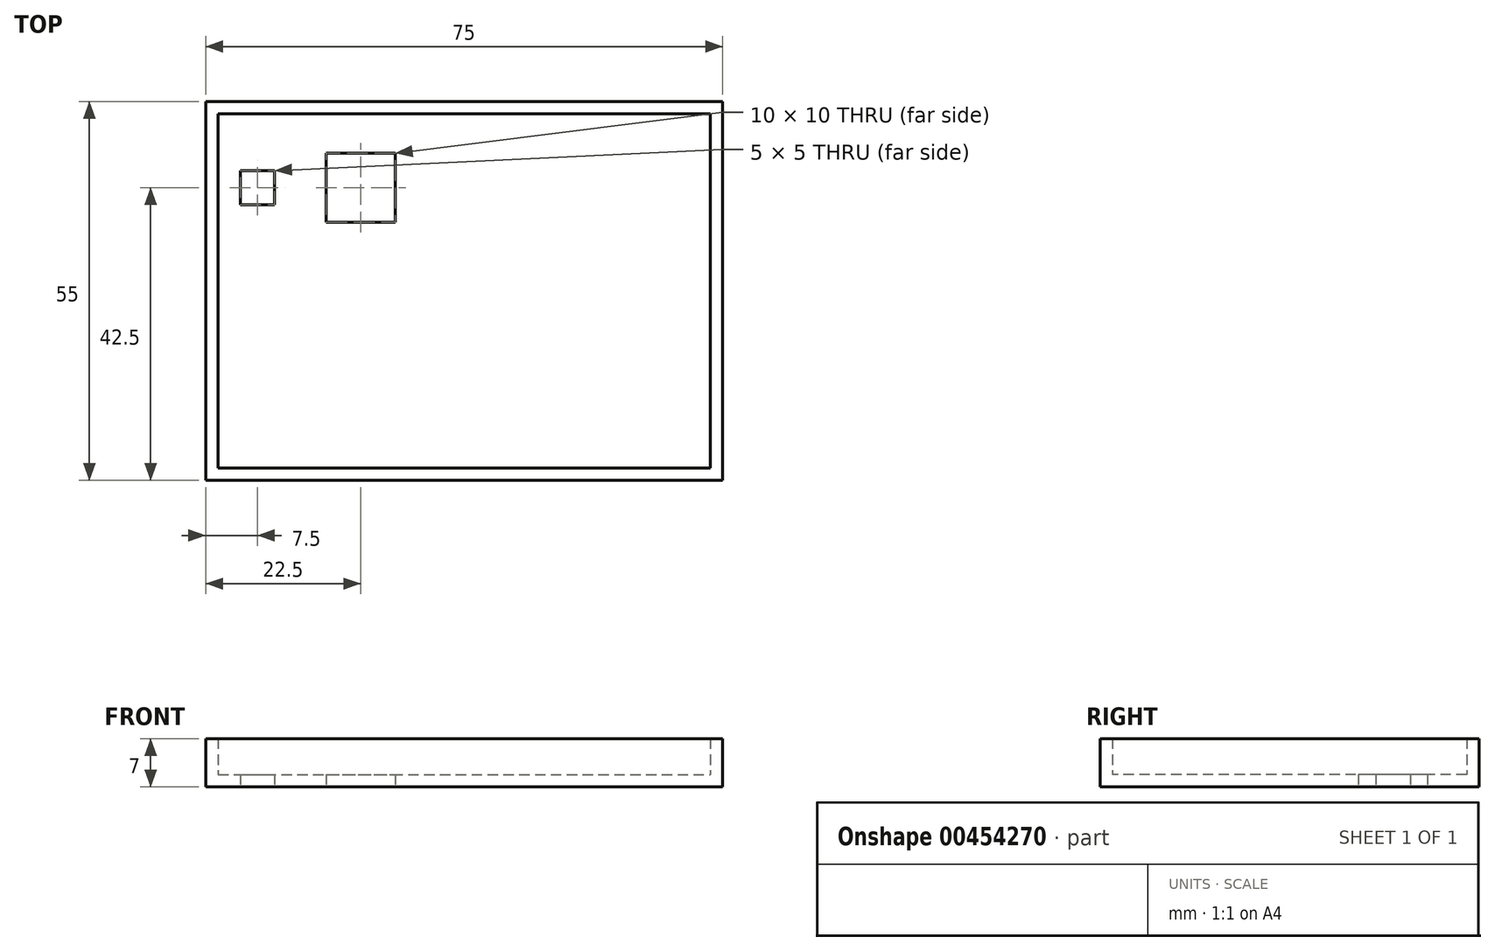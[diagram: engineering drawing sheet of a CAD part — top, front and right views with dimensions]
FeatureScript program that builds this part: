
annotation { "Feature Type Name" : "Feature", "Feature Type Description" : "" }
export const myFeature = defineFeature(function(context is Context, id is Id, definition is map)
    precondition{}
    {
        {
            var Q0;
            Q0=qCreatedBy(makeId("Top.planeOp"),FACE);
            var sketch = newSketch(context, id + "F0", { "sketchPlane" : qUnion([Q0])});
            skLineSegment(sketch, "E0.bottom", {"start": v(-37.5, 27.5) * mm, "end": v(37.5, 27.5) * mm});
            skLineSegment(sketch, "E0.top", {"start": v(-37.5, -27.5) * mm, "end": v(37.5, -27.5) * mm});
            skLineSegment(sketch, "E0.left", {"start": v(-37.5, 27.5) * mm, "end": v(-37.5, -27.5) * mm});
            skLineSegment(sketch, "E0.right", {"start": v(37.5, 27.5) * mm, "end": v(37.5, -27.5) * mm});
            skPoint(sketch, "E0.middle", {"position": v(0, 0) * mm});
            skLineSegment(sketch, "E1.bottom", {"start": v(-32.5, 17.5) * mm, "end": v(-27.5, 17.5) * mm});
            skLineSegment(sketch, "E1.top", {"start": v(-32.5, 12.5) * mm, "end": v(-27.5, 12.5) * mm});
            skLineSegment(sketch, "E1.left", {"start": v(-32.5, 17.5) * mm, "end": v(-32.5, 12.5) * mm});
            skLineSegment(sketch, "E1.right", {"start": v(-27.5, 17.5) * mm, "end": v(-27.5, 12.5) * mm});
            skPoint(sketch, "E1.middle", {"position": v(-30, 15) * mm});
            skLineSegment(sketch, "E2.bottom", {"start": v(-20, 20) * mm, "end": v(-10, 20) * mm});
            skLineSegment(sketch, "E2.top", {"start": v(-20, 10) * mm, "end": v(-10, 10) * mm});
            skLineSegment(sketch, "E2.left", {"start": v(-20, 20) * mm, "end": v(-20, 10) * mm});
            skLineSegment(sketch, "E2.right", {"start": v(-10, 20) * mm, "end": v(-10, 10) * mm});
            skPoint(sketch, "E2.middle", {"position": v(-15, 15) * mm});
            skSolve(sketch);
        }
        {
            var Q0;
            Q0=makeQuery(id+"F0.imprint","IMPRINT",FACE,{"disambiguationData":[TD([[makeQuery(id+"F0.imprint","IMPRINT",EDGE,{"derivedFrom":sQuery(id+"F0.wireOp",EDGE,"E0.bottom")}),-1.0]])]});
            extrude(context, id + "F1", {"entities" : qUnion([Q0]), "depth" : 7 * mm});
        }
        {
            var Q0;
            Q0=makeQuery(id+"F1.opExtrude","CAP_FACE",FACE,{"disambiguationData":[OSD([sQuery(id+"F0.wireOp",EDGE,"E0.bottom"),sQuery(id+"F0.wireOp",EDGE,"E0.top"),sQuery(id+"F0.wireOp",EDGE,"E0.left"),sQuery(id+"F0.wireOp",EDGE,"E0.right"),sQuery(id+"F0.wireOp",EDGE,"E1.bottom"),sQuery(id+"F0.wireOp",EDGE,"E1.top"),sQuery(id+"F0.wireOp",EDGE,"E1.left"),sQuery(id+"F0.wireOp",EDGE,"E1.right"),sQuery(id+"F0.wireOp",EDGE,"E2.bottom"),sQuery(id+"F0.wireOp",EDGE,"E2.top"),sQuery(id+"F0.wireOp",EDGE,"E2.left"),sQuery(id+"F0.wireOp",EDGE,"E2.right")])],"isStart":false});
            shell(context, id + "F2", {"entities" : qUnion([Q0]), "thickness" : 1.8 * mm});
        }
        {
            var Q0;
            Q0=qCreatedBy(makeId("Front.planeOp"),FACE);
            var sketch = newSketch(context, id + "F3", { "sketchPlane" : qUnion([Q0])});
            skLineSegment(sketch, "E3", {"start": v(0, 0) * mm, "end": v(0, 1.8) * mm});
            skLineSegment(sketch, "E4.bottom", {"start": v(0, 1.8) * mm, "end": v(-35, 1.8) * mm});
            skLineSegment(sketch, "E4.top", {"start": v(0, 11.08) * mm, "end": v(-35, 11.08) * mm});
            skLineSegment(sketch, "E4.left", {"start": v(0, 1.8) * mm, "end": v(0, 11.08) * mm});
            skLineSegment(sketch, "E4.right", {"start": v(-35, 1.8) * mm, "end": v(-35, 11.08) * mm});
            skSolve(sketch);
        }
        {
            var Q0;
            Q0=makeQuery(id+"F3.imprint","IMPRINT",FACE,{"disambiguationData":[TD([[makeQuery(id+"F3.imprint","IMPRINT",EDGE,{"derivedFrom":sQuery(id+"F3.wireOp",EDGE,"E4.bottom")}),-1.0]])]});
            extrude(context, id + "F4", {"entities" : qUnion([Q0]), "operationType" : NewBodyOperationType.REMOVE, "oppositeDirection" : true, "depth" : 25 * mm});
        }
    });
